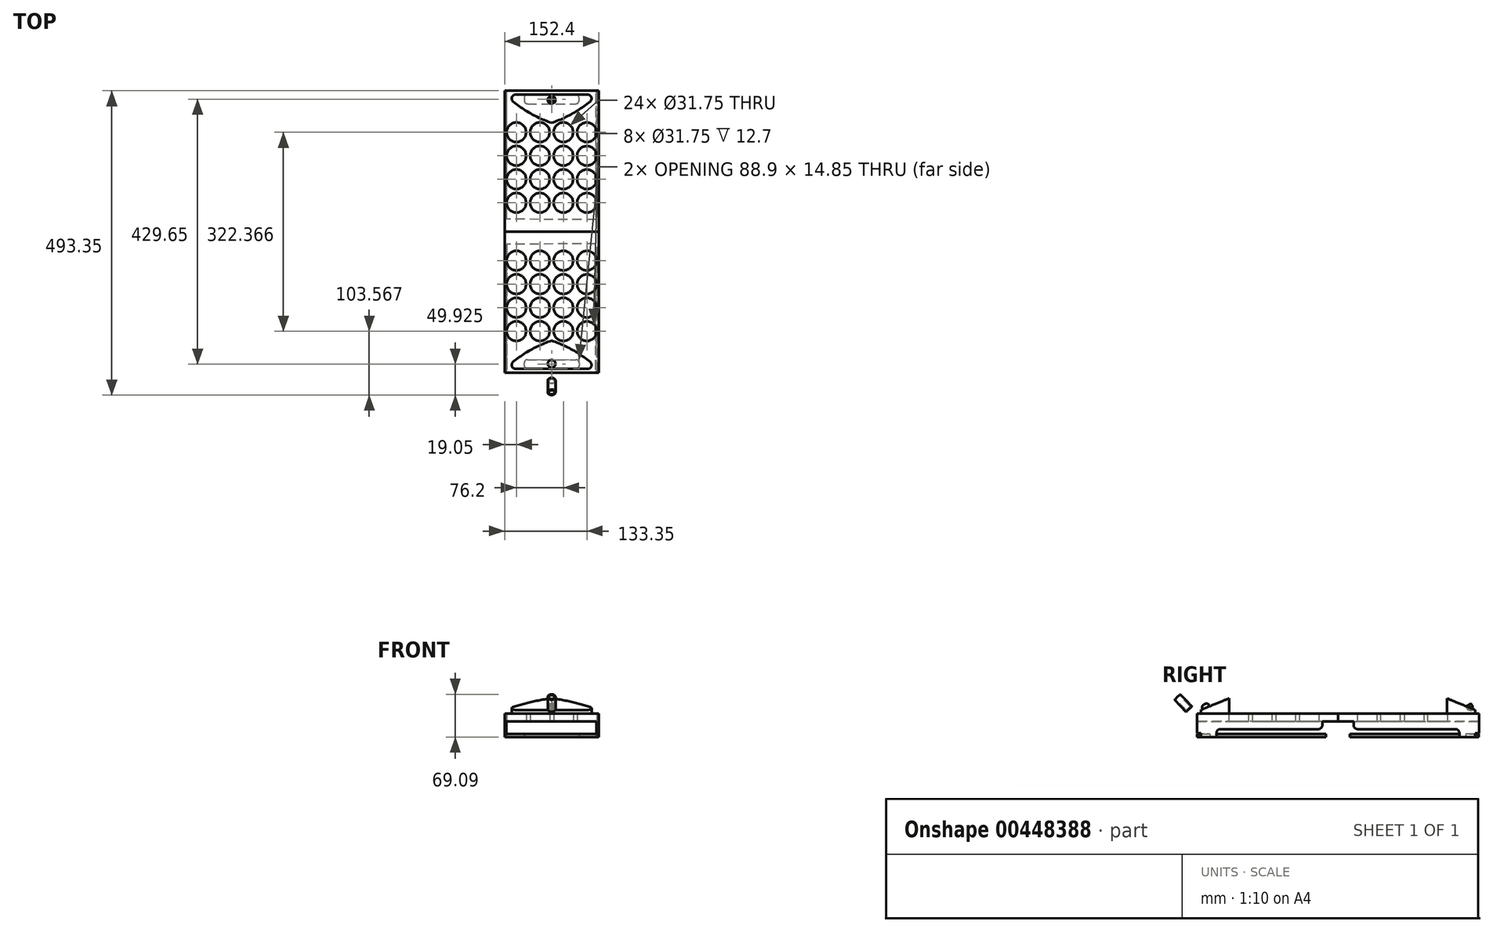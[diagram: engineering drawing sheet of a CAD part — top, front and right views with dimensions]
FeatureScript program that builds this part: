
annotation { "Feature Type Name" : "Feature", "Feature Type Description" : "" }
export const myFeature = defineFeature(function(context is Context, id is Id, definition is map)
    precondition{}
    {
        {
            var Q0;
            Q0=qCreatedBy(makeId("Top.planeOp"),FACE);
            var sketch = newSketch(context, id + "F0", { "sketchPlane" : qUnion([Q0])});
            skLineSegment(sketch, "E0", {"start": v(0, 0) * mm, "end": v(58.42, 0) * mm});
            skArc(sketch, "E1", {"start": v(62.46, 11.25) * mm, "mid": v(32.82, 31.37) * mm, "end": v(0, 45.72) * mm});
            skPoint(sketch, "E2.visualSharp", {"position": v(74.98, 0) * mm});
            skArc(sketch, "E2.filletArc", {"start": v(58.42, 0) * mm, "mid": v(64.4, 4.2) * mm, "end": v(62.46, 11.25) * mm});
            skArc(sketch, "E3.MirrorCS", {"start": v(-62.46, 11.25) * mm, "mid": v(-32.82, 31.37) * mm, "end": v(0, 45.72) * mm});
            skLineSegment(sketch, "E4.MirrorCS", {"start": v(0, 0) * mm, "end": v(-58.42, 0) * mm});
            skArc(sketch, "E5.MirrorCS", {"start": v(-58.42, 0) * mm, "mid": v(-64.4, 4.2) * mm, "end": v(-62.46, 11.25) * mm});
            skSolve(sketch);
        }
        {
            var Q0;
            Q0 = qSketchRegion(id + "F0", true);
            extrude(context, id + "F1", {"entities" : qUnion([Q0]), "depth" : 38.1 * mm});
        }
        {
            var Q0;
            Q0=qCreatedBy(makeId("Right.planeOp"),FACE);
            var sketch = newSketch(context, id + "F2", { "sketchPlane" : qUnion([Q0])});
            skLineSegment(sketch, "E6", {"start": v(53.34, 40.44) * mm, "end": v(-11.5, 40.44) * mm});
            skLineSegment(sketch, "E7", {"start": v(-11.5, 40.44) * mm, "end": v(-11.5, 13.67) * mm});
            skLineSegment(sketch, "E8", {"start": v(-11.5, 13.67) * mm, "end": v(53.34, 40.44) * mm});
            skSolve(sketch);
        }
        {
            var Q0;
            Q0 = qSketchRegion(id + "F2", true);
            extrude(context, id + "F3", {"entities" : qUnion([Q0]), "operationType" : NewBodyOperationType.REMOVE, "endBound" : BoundingType.SYMMETRIC, "oppositeDirection" : true, "depth" : 203.2 * mm});
        }
        {
            var Q0;
            Q0=makeQuery(id+"F1.opExtrude","CAP_EDGE",EDGE,{"disambiguationData":[OSD([sQuery(id+"F0.wireOp",EDGE,"E0"),sQuery(id+"F0.wireOp",EDGE,"E4.MirrorCS")])],"isStart":true});
            cPlane(context, id + "F4", {"entities" : qUnion([Q0]), "cplaneType" : CPlaneType.LINE_ANGLE, "offset" : 25.4 * mm, "angle" : 314 * degree, "width" : 152.4 * mm, "height" : 152.4 * mm});
        }
        {
            var Q0;
            Q0=qCreatedBy(id+"F4.planeOp",FACE);
            var sketch = newSketch(context, id + "F5", { "sketchPlane" : qUnion([Q0])});
            skLineSegment(sketch, "E9", {"start": v(0, 0) * mm, "end": v(0, 0) * mm});
            skCircle(sketch, "E10", {"center": v(0, 0) * mm, "radius": 6.35 * mm});
            skSolve(sketch);
        }
        {
            var Q0;
            Q0 = qSketchRegion(id + "F5", true);
            extrude(context, id + "F6", {"entities" : qUnion([Q0]), "operationType" : NewBodyOperationType.ADD, "oppositeDirection" : true, "depth" : 54.6 * mm, "hasSecondDirection" : true, "secondDirectionOppositeDirection" : true, "secondDirectionDepth" : 27.43 * mm});
        }
        {
            var Q0;
            Q0=makeQuery(id+"F3.boolean.opBoolean","COPY",FACE,{"derivedFrom":makeQuery(id+"F3.opExtrude","SWEPT_FACE",FACE,{"disambiguationData":[OSD([sQuery(id+"F2.wireOp",EDGE,"E8")])]})});
            cPlane(context, id + "F7", {"entities" : qUnion([Q0]), "cplaneType" : CPlaneType.OFFSET, "offset" : 0 * mm, "width" : 152.4 * mm, "height" : 152.4 * mm});
        }
        {
            var Q0;
            Q0=qCreatedBy(id+"F7.planeOp",FACE);
            var sketch = newSketch(context, id + "F8", { "sketchPlane" : qUnion([Q0])});
            skLineSegment(sketch, "E11", {"start": v(0, 0) * mm, "end": v(0, 16.5) * mm, "construction": true});
            skCircle(sketch, "E12", {"center": v(0, 16.51) * mm, "radius": 6.21 * mm});
            skSolve(sketch);
        }
        {
            var Q0;
            Q0 = qSketchRegion(id + "F8", true);
            extrude(context, id + "F9", {"entities" : qUnion([Q0]), "operationType" : NewBodyOperationType.ADD, "depth" : 6.35 * mm});
        }
        {
            var Q0;
            Q0=makeQuery(id+"F9.opExtrude","CAP_EDGE",EDGE,{"disambiguationData":[OSD([sQuery(id+"F8.wireOp",EDGE,"E12")])],"isStart":false});
            fillet(context, id + "F10", {"entities" : qUnion([Q0]), "radius" : 5.08 * mm, "tangentPropagation" : true, "allowEdgeOverflow" : false});
        }
        {
            var Q0;
            Q0=makeQuery(id+"F6.opExtrude","CAP_FACE",FACE,{"disambiguationData":[OSD([sQuery(id+"F5.wireOp",EDGE,"E10")])],"isStart":false});
            var sketch = newSketch(context, id + "F11", { "sketchPlane" : qUnion([Q0])});
            skCircle(sketch, "E13", {"center": v(0, 0) * mm, "radius": 4.56 * mm});
            skSolve(sketch);
        }
        {
            var Q0;
            Q0 = qSketchRegion(id + "F11", true);
            extrude(context, id + "F12", {"entities" : qUnion([Q0]), "operationType" : NewBodyOperationType.REMOVE, "oppositeDirection" : true, "depth" : 25.4 * mm, "hasSecondDirection" : true, "secondDirectionOppositeDirection" : false, "secondDirectionDepth" : 25.65 * mm});
        }
        {
            var Q0;
            Q0=qCreatedBy(makeId("Top.planeOp"),FACE);
            var sketch = newSketch(context, id + "F13", { "sketchPlane" : qUnion([Q0])});
            skLineSegment(sketch, "E14", {"start": v(0, 0) * mm, "end": v(0, -6.35) * mm, "construction": true});
            skLineSegment(sketch, "E15.bottom", {"start": v(-76.2, 222.25) * mm, "end": v(76.2, 222.25) * mm});
            skLineSegment(sketch, "E15.top", {"start": v(-76.2, -6.35) * mm, "end": v(76.2, -6.35) * mm});
            skLineSegment(sketch, "E15.left", {"start": v(-76.2, 222.25) * mm, "end": v(-76.2, -6.35) * mm});
            skLineSegment(sketch, "E15.right", {"start": v(76.2, 222.25) * mm, "end": v(76.2, -6.35) * mm});
            skCircle(sketch, "E16", {"center": v(-57.15, 61.07) * mm, "radius": 15.88 * mm});
            skCircle(sketch, "E17.0.1.0", {"center": v(-57.15, 99.17) * mm, "radius": 15.88 * mm});
            skCircle(sketch, "E17.0.2.0", {"center": v(-57.15, 137.27) * mm, "radius": 15.88 * mm});
            skCircle(sketch, "E17.0.3.0", {"center": v(-57.15, 175.37) * mm, "radius": 15.88 * mm});
            skCircle(sketch, "E17.1.0.0", {"center": v(-19.05, 61.07) * mm, "radius": 15.88 * mm});
            skCircle(sketch, "E17.1.1.0", {"center": v(-19.05, 99.17) * mm, "radius": 15.88 * mm});
            skCircle(sketch, "E17.1.2.0", {"center": v(-19.05, 137.27) * mm, "radius": 15.88 * mm});
            skCircle(sketch, "E17.1.3.0", {"center": v(-19.05, 175.37) * mm, "radius": 15.88 * mm});
            skCircle(sketch, "E17.2.0.0", {"center": v(19.05, 61.07) * mm, "radius": 15.88 * mm});
            skCircle(sketch, "E17.2.1.0", {"center": v(19.05, 99.17) * mm, "radius": 15.88 * mm});
            skCircle(sketch, "E17.2.2.0", {"center": v(19.05, 137.27) * mm, "radius": 15.88 * mm});
            skCircle(sketch, "E17.2.3.0", {"center": v(19.05, 175.37) * mm, "radius": 15.88 * mm});
            skCircle(sketch, "E17.3.0.0", {"center": v(57.15, 61.07) * mm, "radius": 15.88 * mm});
            skCircle(sketch, "E17.3.1.0", {"center": v(57.15, 99.17) * mm, "radius": 15.88 * mm});
            skCircle(sketch, "E17.3.2.0", {"center": v(57.15, 137.27) * mm, "radius": 15.88 * mm});
            skCircle(sketch, "E17.3.3.0", {"center": v(57.15, 175.37) * mm, "radius": 15.88 * mm});
            skLineSegment(sketch, "E17.direction1", {"start": v(-57.15, 61.07) * mm, "end": v(-19.05, 61.07) * mm, "construction": true});
            skLineSegment(sketch, "E17.direction2", {"start": v(-57.15, 61.07) * mm, "end": v(-57.15, 99.17) * mm, "construction": true});
            skLineSegment(sketch, "E18", {"start": v(19.05, 61.07) * mm, "end": v(-19.05, 61.07) * mm, "construction": true});
            skPoint(sketch, "E19", {"position": v(0, 61.07) * mm});
            skSolve(sketch);
        }
        {
            var Q0;
            Q0 = qSketchRegion(id + "F13", true);
            extrude(context, id + "F14", {"entities" : qUnion([Q0]), "operationType" : NewBodyOperationType.ADD, "depth" : 12.7 * mm});
        }
        {
            var Q0;
            Q0=makeQuery(id+"F14.opExtrude","SWEPT_FACE",FACE,{"disambiguationData":[OSD([sQuery(id+"F13.wireOp",EDGE,"E15.right")])]});
            var sketch = newSketch(context, id + "F15", { "sketchPlane" : qUnion([Q0])});
            skLineSegment(sketch, "E20", {"start": v(-6.35, 0) * mm, "end": v(-6.35, -19.05) * mm});
            skLineSegment(sketch, "E21", {"start": v(-6.35, -19.05) * mm, "end": v(0, -19.05) * mm});
            skLineSegment(sketch, "E22", {"start": v(0, -19.05) * mm, "end": v(0, -25.4) * mm});
            skLineSegment(sketch, "E23", {"start": v(196.85, -6.35) * mm, "end": v(196.85, 0) * mm});
            skLineSegment(sketch, "E24", {"start": v(196.85, 0) * mm, "end": v(-6.35, 0) * mm});
            skLineSegment(sketch, "E25", {"start": v(0, -25.4) * mm, "end": v(25.4, -25.4) * mm});
            skLineSegment(sketch, "E26", {"start": v(25.4, -25.4) * mm, "end": v(25.4, -19.05) * mm});
            skLineSegment(sketch, "E27", {"start": v(31.75, -12.7) * mm, "end": v(190.5, -12.7) * mm});
            skPoint(sketch, "E28.visualSharp", {"position": v(25.4, -12.7) * mm});
            skArc(sketch, "E28.filletArc", {"start": v(31.75, -12.7) * mm, "mid": v(27.26, -14.56) * mm, "end": v(25.4, -19.05) * mm});
            skPoint(sketch, "E29.visualSharp", {"position": v(196.85, -12.7) * mm});
            skArc(sketch, "E29.filletArc", {"start": v(190.5, -12.7) * mm, "mid": v(195, -10.84) * mm, "end": v(196.85, -6.35) * mm});
            skSolve(sketch);
        }
        {
            var Q0;
            Q0 = qSketchRegion(id + "F15", true);
            extrude(context, id + "F16", {"entities" : qUnion([Q0]), "operationType" : NewBodyOperationType.ADD, "oppositeDirection" : true, "depth" : 3.8 * mm});
        }
        {
            var Q0;
            Q0=makeQuery(id+"F14.opExtrude","SWEPT_FACE",FACE,{"disambiguationData":[OSD([sQuery(id+"F13.wireOp",EDGE,"E15.left")])]});
            var Q1;
            Q1=makeQuery(id+"F14.opExtrude","CAP_VERTEX",VERTEX,{"disambiguationData":[OSD([sQuery(id+"F13.wireOp",EDGE,"E15.top"),sQuery(id+"F13.wireOp",EDGE,"E15.left")])],"isStart":true});
            cPlane(context, id + "F17", {"entities" : qUnion([Q0, Q1]), "cplaneType" : CPlaneType.PLANE_POINT, "offset" : 25.4 * mm, "width" : 152.4 * mm, "height" : 152.4 * mm});
        }
        {
            var Q0;
            Q0=qCreatedBy(id+"F17.planeOp",FACE);
            var sketch = newSketch(context, id + "F18", { "sketchPlane" : qUnion([Q0])});
            skArc(sketch, "E30.0.0", {"start": v(-196.85, -6.35) * mm, "mid": v(-195, -10.84) * mm, "end": v(-190.5, -12.7) * mm});
            skLineSegment(sketch, "E30.0.1", {"start": v(-190.5, -12.7) * mm, "end": v(-31.75, -12.7) * mm});
            skArc(sketch, "E30.0.2", {"start": v(-31.75, -12.7) * mm, "mid": v(-27.26, -14.56) * mm, "end": v(-25.4, -19.05) * mm});
            skLineSegment(sketch, "E30.0.3", {"start": v(-25.4, -19.05) * mm, "end": v(-25.4, -25.4) * mm});
            skLineSegment(sketch, "E30.0.4", {"start": v(-25.4, -25.4) * mm, "end": v(0, -25.4) * mm});
            skLineSegment(sketch, "E30.0.5", {"start": v(0, -25.4) * mm, "end": v(0, -19.05) * mm});
            skLineSegment(sketch, "E30.0.6", {"start": v(0, -19.05) * mm, "end": v(6.35, -19.05) * mm});
            skLineSegment(sketch, "E30.0.7", {"start": v(6.35, -19.05) * mm, "end": v(6.35, 0) * mm});
            skLineSegment(sketch, "E30.0.8", {"start": v(6.35, 0) * mm, "end": v(-56.62, 0) * mm});
            skLineSegment(sketch, "E30.0.9", {"start": v(-56.62, 0) * mm, "end": v(-65.51, 0) * mm});
            skLineSegment(sketch, "E30.0.10", {"start": v(-65.51, 0) * mm, "end": v(-94.72, 0) * mm});
            skLineSegment(sketch, "E30.0.11", {"start": v(-94.72, 0) * mm, "end": v(-103.61, 0) * mm});
            skLineSegment(sketch, "E30.0.12", {"start": v(-103.61, 0) * mm, "end": v(-132.82, 0) * mm});
            skLineSegment(sketch, "E30.0.13", {"start": v(-132.82, 0) * mm, "end": v(-141.71, 0) * mm});
            skLineSegment(sketch, "E30.0.14", {"start": v(-141.71, 0) * mm, "end": v(-170.92, 0) * mm});
            skLineSegment(sketch, "E30.0.15", {"start": v(-170.92, 0) * mm, "end": v(-179.81, 0) * mm});
            skLineSegment(sketch, "E30.0.16", {"start": v(-179.81, 0) * mm, "end": v(-196.85, 0) * mm});
            skLineSegment(sketch, "E30.0.17", {"start": v(-196.85, 0) * mm, "end": v(-196.85, -6.35) * mm});
            skSolve(sketch);
        }
        {
            var Q0;
            Q0 = qSketchRegion(id + "F18", true);
            extrude(context, id + "F19", {"entities" : qUnion([Q0]), "operationType" : NewBodyOperationType.ADD, "oppositeDirection" : true, "depth" : 2.54 * mm});
        }
        {
            var Q0;
            Q0=makeQuery(id+"F19.opExtrude","CAP_EDGE",EDGE,{"disambiguationData":[OSD([sQuery(id+"F18.wireOp",EDGE,"E30.0.4")])],"isStart":true});
            var Q1;
            Q1=makeQuery(id+"F19.opExtrude","SWEPT_FACE",FACE,{"disambiguationData":[OSD([sQuery(id+"F18.wireOp",EDGE,"E30.0.4")])]});
            cPlane(context, id + "F20", {"entities" : qUnion([Q0, Q1]), "cplaneType" : CPlaneType.LINE_ANGLE, "offset" : 25.4 * mm, "angle" : 0 * degree, "width" : 152.4 * mm, "height" : 152.4 * mm});
        }
        {
            var Q0;
            Q0=qCreatedBy(id+"F20.planeOp",FACE);
            var sketch = newSketch(context, id + "F21", { "sketchPlane" : qUnion([Q0])});
            skLineSegment(sketch, "E31", {"start": v(-76.18, -1.03) * mm, "end": v(-76.18, -6.15) * mm});
            skLineSegment(sketch, "E32", {"start": v(-76.18, -6.15) * mm, "end": v(76.16, -6.15) * mm});
            skLineSegment(sketch, "E33", {"start": v(76.16, -6.15) * mm, "end": v(76.16, -0.97) * mm});
            skLineSegment(sketch, "E34", {"start": v(76.16, -0.97) * mm, "end": v(71.45, -0.97) * mm});
            skLineSegment(sketch, "E35", {"start": v(71.45, -0.97) * mm, "end": v(71.45, 202.71) * mm});
            skLineSegment(sketch, "E36", {"start": v(71.45, 202.71) * mm, "end": v(-72.99, 201.95) * mm});
            skLineSegment(sketch, "E37", {"start": v(-72.99, 201.95) * mm, "end": v(-72.99, -1.03) * mm});
            skLineSegment(sketch, "E38", {"start": v(-72.99, -1.03) * mm, "end": v(-76.18, -1.03) * mm});
            skSolve(sketch);
        }
        {
            var Q0;
            Q0 = qSketchRegion(id + "F21", true);
            extrude(context, id + "F22", {"entities" : qUnion([Q0]), "depth" : 5.08 * mm});
        }
        {
            var Q0;
            Q0=makeQuery(id+"F22.opExtrude","CAP_FACE",FACE,{"disambiguationData":[OSD([sQuery(id+"F21.wireOp",EDGE,"E31"),sQuery(id+"F21.wireOp",EDGE,"E32"),sQuery(id+"F21.wireOp",EDGE,"E33"),sQuery(id+"F21.wireOp",EDGE,"E34"),sQuery(id+"F21.wireOp",EDGE,"E35"),sQuery(id+"F21.wireOp",EDGE,"E36"),sQuery(id+"F21.wireOp",EDGE,"E37"),sQuery(id+"F21.wireOp",EDGE,"E38")])],"isStart":true});
            var sketch = newSketch(context, id + "F23", { "sketchPlane" : qUnion([Q0])});
            skLineSegment(sketch, "E39", {"start": v(0, 0) * mm, "end": v(-39.37, 0) * mm});
            skLineSegment(sketch, "E40", {"start": v(-44.45, -5.08) * mm, "end": v(-44.45, -9.77) * mm});
            skLineSegment(sketch, "E41", {"start": v(-39.37, -14.85) * mm, "end": v(39.37, -14.85) * mm});
            skLineSegment(sketch, "E42", {"start": v(44.45, -9.77) * mm, "end": v(44.45, -5.08) * mm});
            skLineSegment(sketch, "E43", {"start": v(39.37, 0) * mm, "end": v(0, 0) * mm});
            skPoint(sketch, "E44.visualSharp", {"position": v(-44.45, 0) * mm});
            skArc(sketch, "E44.filletArc", {"start": v(-39.37, 0) * mm, "mid": v(-42.96, -1.49) * mm, "end": v(-44.45, -5.08) * mm});
            skPoint(sketch, "E45.visualSharp", {"position": v(-44.45, -14.85) * mm});
            skArc(sketch, "E45.filletArc", {"start": v(-44.45, -9.77) * mm, "mid": v(-42.96, -13.36) * mm, "end": v(-39.37, -14.85) * mm});
            skPoint(sketch, "E46.visualSharp", {"position": v(44.45, 0) * mm});
            skArc(sketch, "E46.filletArc", {"start": v(44.45, -5.08) * mm, "mid": v(42.96, -1.49) * mm, "end": v(39.37, 0) * mm});
            skPoint(sketch, "E47.visualSharp", {"position": v(44.45, -14.85) * mm});
            skArc(sketch, "E47.filletArc", {"start": v(39.37, -14.85) * mm, "mid": v(42.96, -13.36) * mm, "end": v(44.45, -9.77) * mm});
            skSolve(sketch);
        }
        {
            var Q0;
            Q0 = qSketchRegion(id + "F23", true);
            extrude(context, id + "F24", {"entities" : qUnion([Q0]), "operationType" : NewBodyOperationType.REMOVE, "endBound" : BoundingType.UP_TO_NEXT, "oppositeDirection" : true, "depth" : 25.4 * mm});
        }
        {
            var Q0;
            Q0=makeQuery(id+"F1.opExtrude","SWEPT_BODY",BODY,{"disambiguationData":[OSD([sQuery(id+"F0.wireOp",EDGE,"E0"),sQuery(id+"F0.wireOp",EDGE,"E1"),sQuery(id+"F0.wireOp",EDGE,"E2.filletArc"),sQuery(id+"F0.wireOp",EDGE,"E3.MirrorCS"),sQuery(id+"F0.wireOp",EDGE,"E4.MirrorCS"),sQuery(id+"F0.wireOp",EDGE,"E5.MirrorCS")])]});
            var Q1;
            Q1=makeQuery(id+"F22.opExtrude","SWEPT_BODY",BODY,{"disambiguationData":[OSD([sQuery(id+"F21.wireOp",EDGE,"E31"),sQuery(id+"F21.wireOp",EDGE,"E32"),sQuery(id+"F21.wireOp",EDGE,"E33"),sQuery(id+"F21.wireOp",EDGE,"E34"),sQuery(id+"F21.wireOp",EDGE,"E35"),sQuery(id+"F21.wireOp",EDGE,"E36"),sQuery(id+"F21.wireOp",EDGE,"E37"),sQuery(id+"F21.wireOp",EDGE,"E38")])]});
            var Q2;
            Q2=makeQuery(id+"F14.opExtrude","SWEPT_FACE",FACE,{"disambiguationData":[OSD([sQuery(id+"F13.wireOp",EDGE,"E15.bottom")])]});
            mirror(context, id + "F25", {"operationType" : NewBodyOperationType.ADD, "entities" : qUnion([Q0, Q1]), "mirrorPlane" : qUnion([Q2])});
        }
    });
